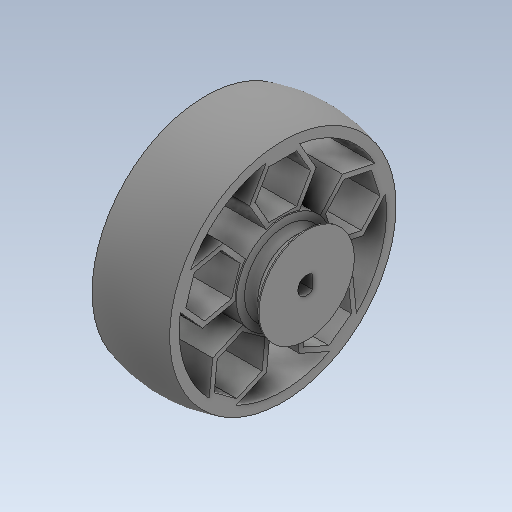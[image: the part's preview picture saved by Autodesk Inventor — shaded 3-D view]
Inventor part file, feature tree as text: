
AUTODESK INVENTOR PART (.ipt)
format: ipt  version: 2020 (Build 240168000, 168)  size: 415,232 bytes
history: native  units: in
note: dims shown in document units (in); Inventor stores cm internally (conversion verified against a paired STEP export)
features: sketch x4, extrude x2, revolve x2, projected_geometry x1
ambient origin geometry x8: Origin, YZ Plane, XZ Plane, XY Plane, X Axis, Y Axis, Z Axis, Center Point
bodies: Solid1 (feature_tree)
feature tree (9):
  extrude  "Extrusion1"  Depth=0.0394in
  sketch  "Sketch3"  dims[d6=0.6299in d7=0.1575in]
  revolve  "Revolution1"  [1 undecoded]
  extrude  "Extrusion2"  Depth=0.1575in
  revolve  "Revolution2"  [1 undecoded]
  sketch  "Sketch1"  dims[d0=0.1181in d1=0.0394in]
  sketch  "Sketch2"  dims[d3=1.4961in d4=0.1181in]
  projected_geometry  "Projected Loop1"
  sketch  "Sketch4"  dims[d8=0.0in d9=1.4961in d10=0.063in d11=0.0315in d16=0.5118in d17=0.0in d19=360.0deg d20=0.0787in d24=0.0394in d25=90.0deg d26=45.0deg d28=0.0079in d29=1.9685in d31=360.0deg]
note: 2 required parameter values undecoded (feature->parameter linkage not recoverable at this tier; creation-order binding heuristic only, values carry confidence <= 0.55)
